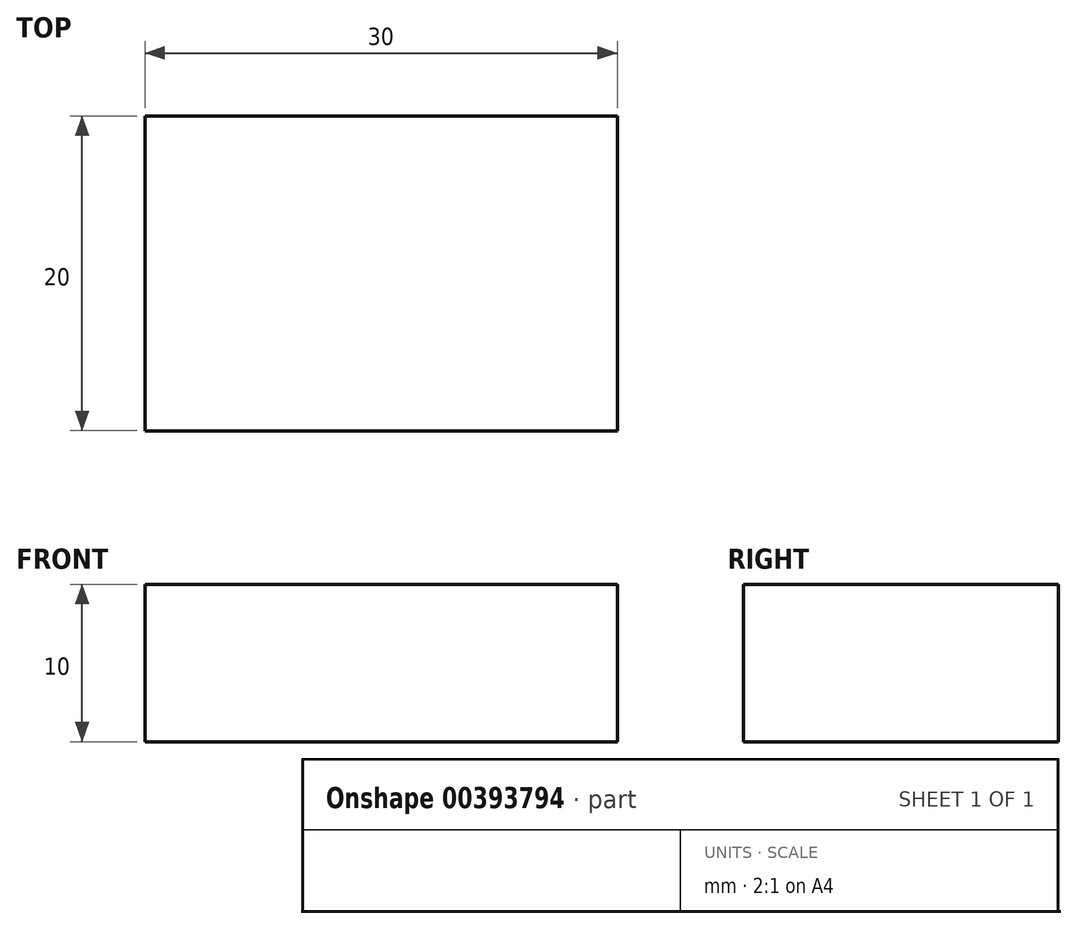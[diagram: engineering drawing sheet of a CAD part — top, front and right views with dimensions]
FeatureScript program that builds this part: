
annotation { "Feature Type Name" : "Feature", "Feature Type Description" : "" }
export const myFeature = defineFeature(function(context is Context, id is Id, definition is map)
    precondition{}
    {
        {
            var Q0;
            Q0=qCreatedBy(makeId("Top.planeOp"),FACE);
            var sketch = newSketch(context, id + "F0", { "sketchPlane" : qUnion([Q0])});
            skLineSegment(sketch, "E0.bottom", {"start": v(-16.18, 8.33) * mm, "end": v(13.82, 8.33) * mm});
            skLineSegment(sketch, "E0.top", {"start": v(-16.18, -11.67) * mm, "end": v(13.82, -11.67) * mm});
            skLineSegment(sketch, "E0.left", {"start": v(-16.18, 8.33) * mm, "end": v(-16.18, -11.67) * mm});
            skLineSegment(sketch, "E0.right", {"start": v(13.82, 8.33) * mm, "end": v(13.82, -11.67) * mm});
            skSolve(sketch);
        }
        {
            var Q0;
            Q0 = qSketchRegion(id + "F0", true);
            extrude(context, id + "F1", {"entities" : qUnion([Q0]), "depth" : 10 * mm});
        }
    });
